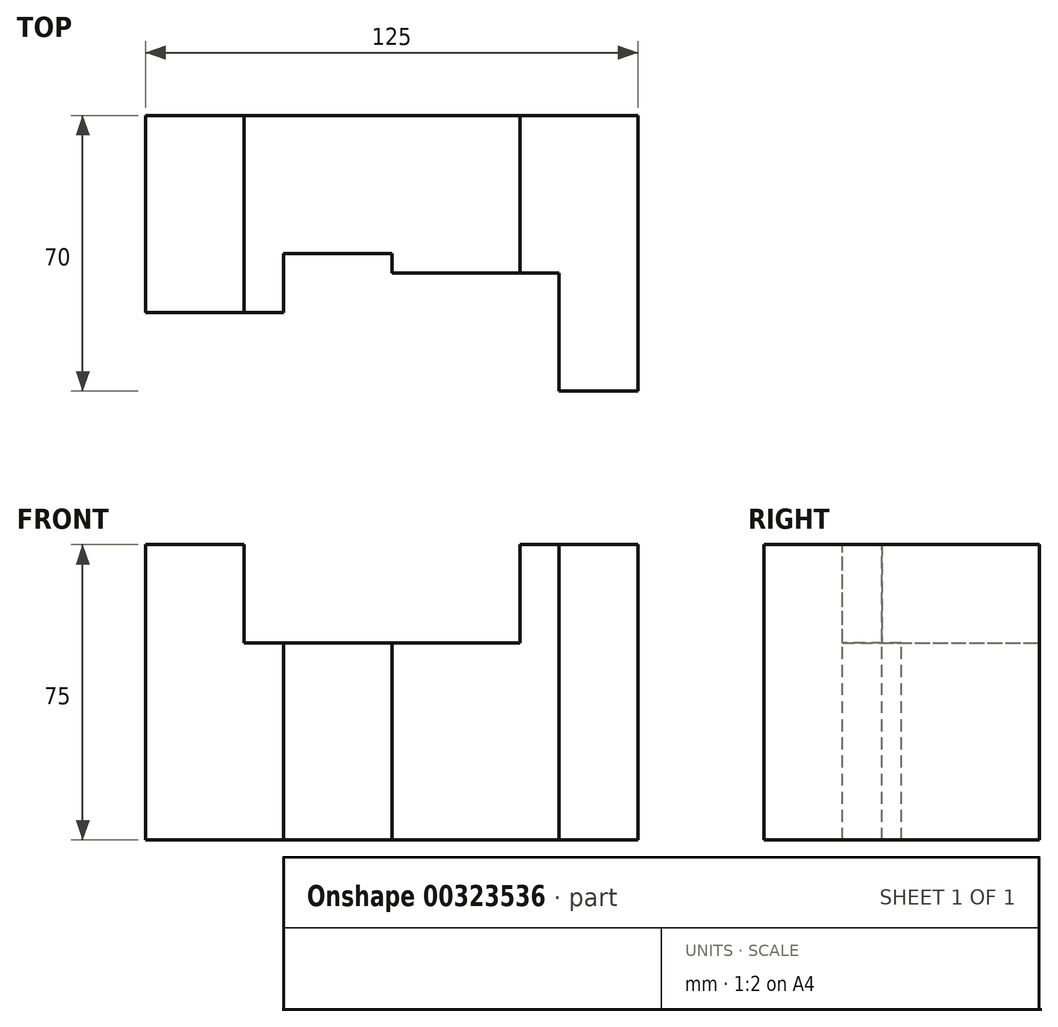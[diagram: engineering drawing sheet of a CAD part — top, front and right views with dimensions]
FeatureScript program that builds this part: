
annotation { "Feature Type Name" : "Feature", "Feature Type Description" : "" }
export const myFeature = defineFeature(function(context is Context, id is Id, definition is map)
    precondition{}
    {
        {
            var Q0;
            Q0=qCreatedBy(makeId("Right.planeOp"),FACE);
            var sketch = newSketch(context, id + "F0", { "sketchPlane" : qUnion([Q0])});
            skLineSegment(sketch, "E0", {"start": v(-35, 0) * mm, "end": v(35, 0) * mm});
            skLineSegment(sketch, "E1", {"start": v(35, 0) * mm, "end": v(35, 75) * mm});
            skLineSegment(sketch, "E2", {"start": v(35, 75) * mm, "end": v(-35, 75) * mm});
            skLineSegment(sketch, "E3", {"start": v(-35, 75) * mm, "end": v(-35, 0) * mm});
            skSolve(sketch);
        }
        {
            var Q0;
            Q0 = qSketchRegion(id + "F0", true);
            extrude(context, id + "F1", {"entities" : qUnion([Q0]), "endBound" : BoundingType.SYMMETRIC, "depth" : 125 * mm});
        }
        {
            var Q0;
            Q0=makeQuery(id+"F1.opExtrude","SWEPT_FACE",FACE,{"disambiguationData":[OSD([sQuery(id+"F0.wireOp",EDGE,"E2")])]});
            var sketch = newSketch(context, id + "F2", { "sketchPlane" : qUnion([Q0])});
            skLineSegment(sketch, "E4", {"start": v(-62.5, -35) * mm, "end": v(42.5, -35) * mm});
            skLineSegment(sketch, "E5", {"start": v(42.5, -35) * mm, "end": v(42.5, -5) * mm});
            skLineSegment(sketch, "E6", {"start": v(-62.5, -15) * mm, "end": v(-62.5, -35) * mm});
            skLineSegment(sketch, "E7", {"start": v(42.5, -5) * mm, "end": v(0, -5) * mm});
            skLineSegment(sketch, "E8", {"start": v(0, -5) * mm, "end": v(0, 0) * mm});
            skLineSegment(sketch, "E9", {"start": v(0, 0) * mm, "end": v(-27.5, 0) * mm});
            skLineSegment(sketch, "E10", {"start": v(-27.5, 0) * mm, "end": v(-27.5, -15) * mm});
            skLineSegment(sketch, "E11", {"start": v(-27.5, -15) * mm, "end": v(-62.5, -15) * mm});
            skSolve(sketch);
        }
        {
            var Q0;
            Q0 = qSketchRegion(id + "F2", true);
            extrude(context, id + "F3", {"entities" : qUnion([Q0]), "operationType" : NewBodyOperationType.REMOVE, "endBound" : BoundingType.THROUGH_ALL, "oppositeDirection" : true, "depth" : 25 * mm});
        }
        {
            var Q0;
            Q0=makeQuery(id+"F1.opExtrude","SWEPT_FACE",FACE,{"disambiguationData":[OSD([sQuery(id+"F0.wireOp",EDGE,"E1")])]});
            var sketch = newSketch(context, id + "F4", { "sketchPlane" : qUnion([Q0])});
            skLineSegment(sketch, "E12", {"start": v(-32.5, 75) * mm, "end": v(-32.5, 50) * mm});
            skLineSegment(sketch, "E13", {"start": v(-32.5, 50) * mm, "end": v(37.5, 50) * mm});
            skLineSegment(sketch, "E14", {"start": v(37.5, 50) * mm, "end": v(37.5, 75) * mm});
            skLineSegment(sketch, "E15", {"start": v(37.5, 75) * mm, "end": v(-32.5, 75) * mm});
            skSolve(sketch);
        }
        {
            var Q0;
            Q0 = qSketchRegion(id + "F4", true);
            extrude(context, id + "F5", {"entities" : qUnion([Q0]), "operationType" : NewBodyOperationType.REMOVE, "endBound" : BoundingType.THROUGH_ALL, "oppositeDirection" : true, "depth" : 25 * mm});
        }
    });
